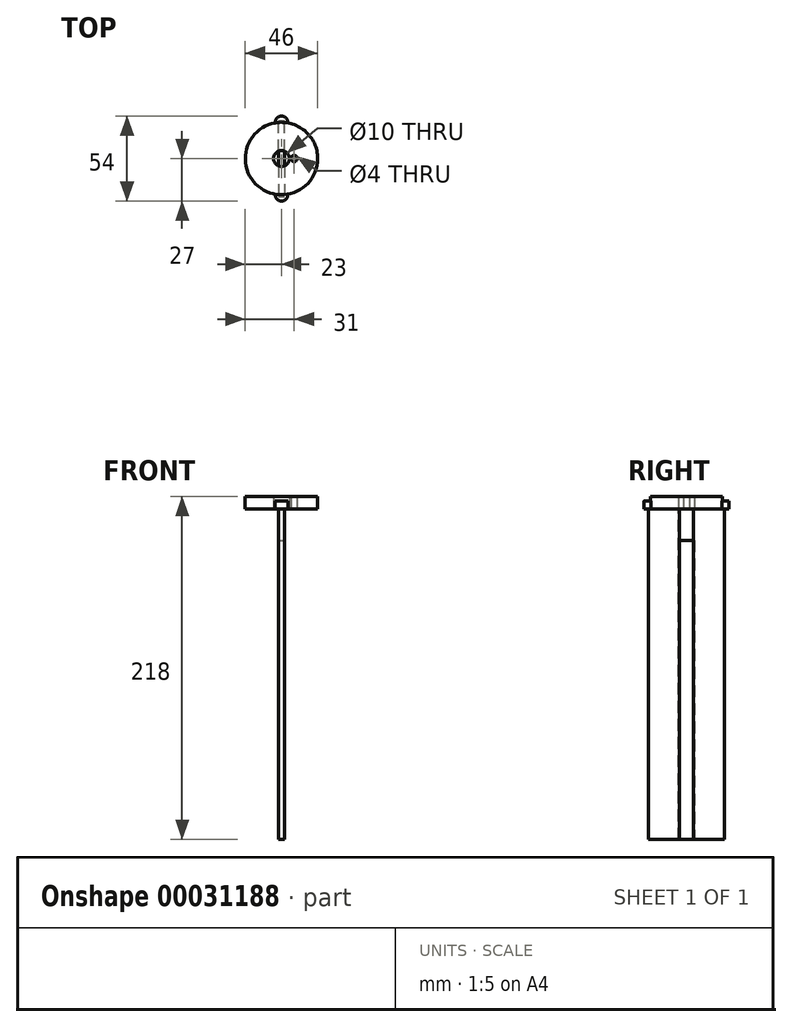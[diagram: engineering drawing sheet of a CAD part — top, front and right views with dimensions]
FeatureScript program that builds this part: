
annotation { "Feature Type Name" : "Feature", "Feature Type Description" : "" }
export const myFeature = defineFeature(function(context is Context, id is Id, definition is map)
    precondition{}
    {
        {
            var Q0;
            Q0=qCreatedBy(makeId("Top.planeOp"),FACE);
            var sketch = newSketch(context, id + "F0", { "sketchPlane" : qUnion([Q0])});
            skArc(sketch, "E0", {"start": v(-3.98, 22.65) * mm, "mid": v(-23, 0) * mm, "end": v(-3.98, -22.65) * mm});
            skArc(sketch, "E1", {"start": v(3.98, 22.65) * mm, "mid": v(0, 27) * mm, "end": v(-3.98, 22.65) * mm});
            skLineSegment(sketch, "E2", {"start": v(0, 0) * mm, "end": v(-23, 0) * mm, "construction": true});
            skArc(sketch, "E3.MirrorC", {"start": v(3.98, -22.65) * mm, "mid": v(0, -27) * mm, "end": v(-3.98, -22.65) * mm});
            skArc(sketch, "E4.trimOffspring", {"start": v(3.98, -22.65) * mm, "mid": v(23, 0) * mm, "end": v(3.98, 22.65) * mm});
            skCircle(sketch, "E5", {"center": v(0, 0) * mm, "radius": 5 * mm});
            skCircle(sketch, "E6", {"center": v(8, 0) * mm, "radius": 2 * mm});
            skSolve(sketch);
        }
        {
            var Q0;
            Q0 = qSketchRegion(id + "F0", true);
            extrude(context, id + "F1", {"entities" : qUnion([Q0]), "depth" : 8 * mm});
        }
        {
            var Q0;
            Q0=makeQuery(id+"F1.opExtrude","CAP_FACE",FACE,{"disambiguationData":[OSD([sQuery(id+"F0.wireOp",EDGE,"E0"),sQuery(id+"F0.wireOp",EDGE,"E1"),sQuery(id+"F0.wireOp",EDGE,"E3.MirrorC"),sQuery(id+"F0.wireOp",EDGE,"E4.trimOffspring")])],"isStart":false});
            var sketch = newSketch(context, id + "F2", { "sketchPlane" : qUnion([Q0])});
            skArc(sketch, "E7.0", {"start": v(3.98, 22.65) * mm, "mid": v(0, 27) * mm, "end": v(-3.98, 22.65) * mm});
            skArc(sketch, "E8.0", {"start": v(3.98, -22.65) * mm, "mid": v(0, -27) * mm, "end": v(-3.98, -22.65) * mm});
            skArc(sketch, "E9", {"start": v(-3.98, -22.65) * mm, "mid": v(0, -23) * mm, "end": v(3.98, -22.65) * mm});
            skArc(sketch, "E10.trimOffspring", {"start": v(3.98, 22.65) * mm, "mid": v(0, 23) * mm, "end": v(-3.98, 22.65) * mm});
            skSolve(sketch);
        }
        {
            var Q0;
            Q0 = qSketchRegion(id + "F2", true);
            extrude(context, id + "F3", {"entities" : qUnion([Q0]), "operationType" : NewBodyOperationType.REMOVE, "oppositeDirection" : true, "depth" : 3 * mm});
        }
        {
            var Q0;
            Q0=makeQuery(id+"F1.opExtrude","CAP_FACE",FACE,{"disambiguationData":[OSD([sQuery(id+"F0.wireOp",EDGE,"E0"),sQuery(id+"F0.wireOp",EDGE,"E1"),sQuery(id+"F0.wireOp",EDGE,"E3.MirrorC"),sQuery(id+"F0.wireOp",EDGE,"E4.trimOffspring"),sQuery(id+"F0.wireOp",EDGE,"E5")])],"isStart":true});
            var sketch = newSketch(context, id + "F4", { "sketchPlane" : qUnion([Q0])});
            skLineSegment(sketch, "E11.top", {"start": v(-2, -24) * mm, "end": v(2, -24) * mm});
            skLineSegment(sketch, "E11.left", {"start": v(-2, 0) * mm, "end": v(-2, -24) * mm});
            skLineSegment(sketch, "E11.right", {"start": v(2, -1.5) * mm, "end": v(2, -24) * mm});
            skLineSegment(sketch, "E12.MirrorCS", {"start": v(2, 1.5) * mm, "end": v(2, 24) * mm});
            skLineSegment(sketch, "E13.MirrorCS", {"start": v(-2, 0) * mm, "end": v(-2, 24) * mm});
            skLineSegment(sketch, "E14.MirrorCS", {"start": v(-2, 24) * mm, "end": v(2, 24) * mm});
            skPoint(sketch, "E15.orphan", {"position": v(2, 0) * mm});
            skLineSegment(sketch, "E16", {"start": v(2, 1.5) * mm, "end": v(2, -1.5) * mm});
            skSolve(sketch);
        }
        {
            var Q0;
            Q0=makeQuery(id+"F4.imprint","IMPRINT",FACE,{"disambiguationData":[TD([[makeQuery(id+"F4.imprint","IMPRINT",EDGE,{"derivedFrom":sQuery(id+"F4.wireOp",EDGE,"E11.top")}),1.0]])]});
            var Q1;
            {var subQ5=sQuery(id+"F4.wireOp",EDGE,"E14.MirrorCS");Q1=makeQuery(id+"F4.imprint","IMPRINT",FACE,{"disambiguationData":[TD([[makeQuery(id+"F4.imprint","IMPRINT",EDGE,{"derivedFrom":subQ5}),-1.0]])]});}
            extrude(context, id + "F5", {"entities" : qUnion([Q0, Q1]), "depth" : 210 * mm});
        }
        {
            var Q0;
            Q0=makeQuery(id+"F5.opExtrude","CAP_FACE",FACE,{"disambiguationData":[OSD([sQuery(id+"F0.wireOp",EDGE,"E5"),sQuery(id+"F4.wireOp",EDGE,"E12.MirrorCS"),sQuery(id+"F4.wireOp",EDGE,"E13.MirrorCS"),sQuery(id+"F4.wireOp",EDGE,"E14.MirrorCS")])],"isStart":false});
            var sketch = newSketch(context, id + "F6", { "sketchPlane" : qUnion([Q0])});
            skArc(sketch, "E17.0", {"start": v(-2, 4.58) * mm, "mid": v(0, 5) * mm, "end": v(2, 4.58) * mm});
            skArc(sketch, "E18.0", {"start": v(2, -4.58) * mm, "mid": v(0, -5) * mm, "end": v(-2, -4.58) * mm});
            skLineSegment(sketch, "E19", {"start": v(2, 4.58) * mm, "end": v(2, -4.58) * mm});
            skLineSegment(sketch, "E20", {"start": v(-2, 4.58) * mm, "end": v(-2, -4.58) * mm});
            skSolve(sketch);
        }
        {
            var Q0;
            Q0 = qSketchRegion(id + "F6", true);
            var Q1;
            Q1=makeQuery(id+"F6.imprint","IMPRINT",FACE,{"disambiguationData":[TD([[makeQuery(id+"F6.imprint","IMPRINT",EDGE,{"derivedFrom":sQuery(id+"F6.wireOp",EDGE,"E17.0")}),-1.0]])]});
            extrude(context, id + "F7", {"entities" : qUnion([Q0, Q1]), "oppositeDirection" : true, "depth" : 190 * mm});
        }
    });
